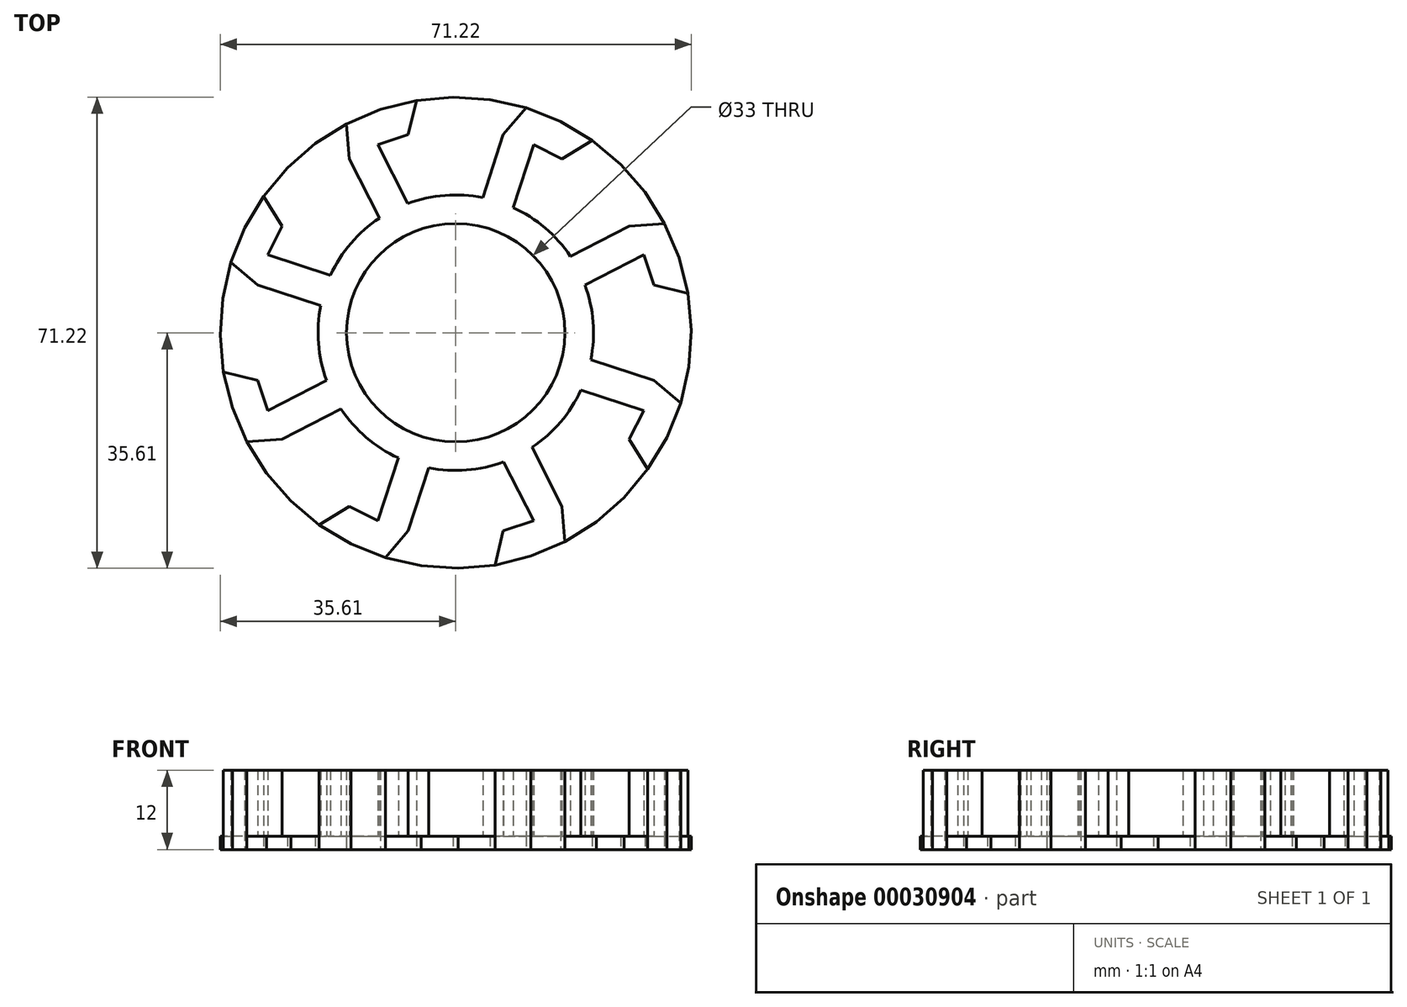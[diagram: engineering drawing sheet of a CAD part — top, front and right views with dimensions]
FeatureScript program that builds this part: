
annotation { "Feature Type Name" : "Feature", "Feature Type Description" : "" }
export const myFeature = defineFeature(function(context is Context, id is Id, definition is map)
    precondition{}
    {
        {
            var Q0;
            Q0=qCreatedBy(makeId("Top.planeOp"),FACE);
            var sketch = newSketch(context, id + "F0", { "sketchPlane" : qUnion([Q0])});
            skCircle(sketch, "E0.cCircle", {"center": v(0, 0) * mm, "radius": 30.68 * mm, "construction": true});
            skLineSegment(sketch, "E0.0", {"start": v(30.68, 2.41) * mm, "end": v(30.68, -2.41) * mm});
            skLineSegment(sketch, "E0.1", {"start": v(30.68, -2.41) * mm, "end": v(29.92, -7.18) * mm});
            skLineSegment(sketch, "E0.2", {"start": v(29.92, -7.18) * mm, "end": v(28.43, -11.78) * mm});
            skLineSegment(sketch, "E0.3", {"start": v(28.43, -11.78) * mm, "end": v(26.24, -16.08) * mm});
            skLineSegment(sketch, "E0.4", {"start": v(26.24, -16.08) * mm, "end": v(23.4, -19.98) * mm});
            skLineSegment(sketch, "E0.5", {"start": v(23.4, -19.98) * mm, "end": v(19.98, -23.4) * mm});
            skLineSegment(sketch, "E0.6", {"start": v(19.98, -23.4) * mm, "end": v(16.08, -26.24) * mm});
            skLineSegment(sketch, "E0.7", {"start": v(16.08, -26.24) * mm, "end": v(11.78, -28.43) * mm});
            skLineSegment(sketch, "E0.8", {"start": v(11.78, -28.43) * mm, "end": v(7.18, -29.92) * mm});
            skLineSegment(sketch, "E0.9", {"start": v(7.18, -29.92) * mm, "end": v(2.41, -30.68) * mm});
            skLineSegment(sketch, "E0.10", {"start": v(2.41, -30.68) * mm, "end": v(-2.41, -30.68) * mm});
            skLineSegment(sketch, "E0.11", {"start": v(-2.41, -30.68) * mm, "end": v(-7.18, -29.92) * mm});
            skLineSegment(sketch, "E0.12", {"start": v(-7.18, -29.92) * mm, "end": v(-11.78, -28.43) * mm});
            skLineSegment(sketch, "E0.13", {"start": v(-11.78, -28.43) * mm, "end": v(-16.08, -26.24) * mm});
            skLineSegment(sketch, "E0.14", {"start": v(-16.08, -26.24) * mm, "end": v(-19.98, -23.4) * mm});
            skLineSegment(sketch, "E0.15", {"start": v(-19.98, -23.4) * mm, "end": v(-23.4, -19.98) * mm});
            skLineSegment(sketch, "E0.16", {"start": v(-23.4, -19.98) * mm, "end": v(-26.24, -16.08) * mm});
            skLineSegment(sketch, "E0.17", {"start": v(-26.24, -16.08) * mm, "end": v(-28.43, -11.78) * mm});
            skLineSegment(sketch, "E0.18", {"start": v(-28.43, -11.78) * mm, "end": v(-29.92, -7.18) * mm});
            skLineSegment(sketch, "E0.19", {"start": v(-29.92, -7.18) * mm, "end": v(-30.68, -2.41) * mm});
            skLineSegment(sketch, "E0.20", {"start": v(-30.68, -2.41) * mm, "end": v(-30.68, 2.41) * mm});
            skLineSegment(sketch, "E0.21", {"start": v(-30.68, 2.41) * mm, "end": v(-29.92, 7.18) * mm});
            skLineSegment(sketch, "E0.22", {"start": v(-29.92, 7.18) * mm, "end": v(-28.43, 11.78) * mm});
            skLineSegment(sketch, "E0.23", {"start": v(-28.43, 11.78) * mm, "end": v(-26.24, 16.08) * mm});
            skLineSegment(sketch, "E0.24", {"start": v(-26.24, 16.08) * mm, "end": v(-23.4, 19.98) * mm});
            skLineSegment(sketch, "E0.25", {"start": v(-23.4, 19.98) * mm, "end": v(-19.98, 23.4) * mm});
            skLineSegment(sketch, "E0.26", {"start": v(-19.98, 23.4) * mm, "end": v(-16.08, 26.24) * mm});
            skLineSegment(sketch, "E0.27", {"start": v(-16.08, 26.24) * mm, "end": v(-11.78, 28.43) * mm});
            skLineSegment(sketch, "E0.28", {"start": v(-11.78, 28.43) * mm, "end": v(-7.18, 29.92) * mm});
            skLineSegment(sketch, "E0.29", {"start": v(-7.18, 29.92) * mm, "end": v(-2.41, 30.68) * mm});
            skLineSegment(sketch, "E0.30", {"start": v(-2.41, 30.68) * mm, "end": v(2.41, 30.68) * mm});
            skLineSegment(sketch, "E0.31", {"start": v(2.41, 30.68) * mm, "end": v(7.18, 29.92) * mm});
            skLineSegment(sketch, "E0.32", {"start": v(7.18, 29.92) * mm, "end": v(11.78, 28.43) * mm});
            skLineSegment(sketch, "E0.33", {"start": v(11.78, 28.43) * mm, "end": v(16.08, 26.24) * mm});
            skLineSegment(sketch, "E0.34", {"start": v(16.08, 26.24) * mm, "end": v(19.98, 23.4) * mm});
            skLineSegment(sketch, "E0.35", {"start": v(19.98, 23.4) * mm, "end": v(23.4, 19.98) * mm});
            skLineSegment(sketch, "E0.36", {"start": v(23.4, 19.98) * mm, "end": v(26.24, 16.08) * mm});
            skLineSegment(sketch, "E0.37", {"start": v(26.24, 16.08) * mm, "end": v(28.43, 11.78) * mm});
            skLineSegment(sketch, "E0.38", {"start": v(28.43, 11.78) * mm, "end": v(29.92, 7.18) * mm});
            skLineSegment(sketch, "E0.39", {"start": v(29.92, 7.18) * mm, "end": v(30.68, 2.41) * mm});
            skPoint(sketch, "E0.0.midPoint", {"position": v(30.68, 0) * mm});
            skCircle(sketch, "E1.cCircle", {"center": v(0, 0) * mm, "radius": 35.5 * mm, "construction": true});
            skLineSegment(sketch, "E1.0", {"start": v(-0.37, 35.61) * mm, "end": v(5.2, 35.23) * mm});
            skLineSegment(sketch, "E1.1", {"start": v(5.2, 35.23) * mm, "end": v(10.65, 33.98) * mm});
            skLineSegment(sketch, "E1.2", {"start": v(10.65, 33.98) * mm, "end": v(15.83, 31.9) * mm});
            skLineSegment(sketch, "E1.3", {"start": v(15.83, 31.9) * mm, "end": v(20.63, 29.03) * mm});
            skLineSegment(sketch, "E1.4", {"start": v(20.63, 29.03) * mm, "end": v(24.92, 25.45) * mm});
            skLineSegment(sketch, "E1.5", {"start": v(24.92, 25.45) * mm, "end": v(28.6, 21.23) * mm});
            skLineSegment(sketch, "E1.6", {"start": v(28.6, 21.23) * mm, "end": v(31.56, 16.5) * mm});
            skLineSegment(sketch, "E1.7", {"start": v(31.56, 16.5) * mm, "end": v(33.75, 11.36) * mm});
            skLineSegment(sketch, "E1.8", {"start": v(33.75, 11.36) * mm, "end": v(35.11, 5.94) * mm});
            skLineSegment(sketch, "E1.9", {"start": v(35.11, 5.94) * mm, "end": v(35.61, 0.37) * mm});
            skLineSegment(sketch, "E1.10", {"start": v(35.61, 0.37) * mm, "end": v(35.23, -5.2) * mm});
            skLineSegment(sketch, "E1.11", {"start": v(35.23, -5.2) * mm, "end": v(33.98, -10.65) * mm});
            skLineSegment(sketch, "E1.12", {"start": v(33.98, -10.65) * mm, "end": v(31.9, -15.83) * mm});
            skLineSegment(sketch, "E1.13", {"start": v(31.9, -15.83) * mm, "end": v(29.03, -20.63) * mm});
            skLineSegment(sketch, "E1.14", {"start": v(29.03, -20.63) * mm, "end": v(25.45, -24.92) * mm});
            skLineSegment(sketch, "E1.15", {"start": v(25.45, -24.92) * mm, "end": v(21.23, -28.6) * mm});
            skLineSegment(sketch, "E1.16", {"start": v(21.23, -28.6) * mm, "end": v(16.5, -31.56) * mm});
            skLineSegment(sketch, "E1.17", {"start": v(16.5, -31.56) * mm, "end": v(11.36, -33.75) * mm});
            skLineSegment(sketch, "E1.18", {"start": v(11.36, -33.75) * mm, "end": v(5.94, -35.11) * mm});
            skLineSegment(sketch, "E1.19", {"start": v(5.94, -35.11) * mm, "end": v(0.37, -35.61) * mm});
            skLineSegment(sketch, "E1.20", {"start": v(0.37, -35.61) * mm, "end": v(-5.2, -35.23) * mm});
            skLineSegment(sketch, "E1.21", {"start": v(-5.2, -35.23) * mm, "end": v(-10.65, -33.98) * mm});
            skLineSegment(sketch, "E1.22", {"start": v(-10.65, -33.98) * mm, "end": v(-15.83, -31.9) * mm});
            skLineSegment(sketch, "E1.23", {"start": v(-15.83, -31.9) * mm, "end": v(-20.63, -29.03) * mm});
            skLineSegment(sketch, "E1.24", {"start": v(-20.63, -29.03) * mm, "end": v(-24.92, -25.45) * mm});
            skLineSegment(sketch, "E1.25", {"start": v(-24.92, -25.45) * mm, "end": v(-28.6, -21.23) * mm});
            skLineSegment(sketch, "E1.26", {"start": v(-28.6, -21.23) * mm, "end": v(-31.56, -16.5) * mm});
            skLineSegment(sketch, "E1.27", {"start": v(-31.56, -16.5) * mm, "end": v(-33.75, -11.36) * mm});
            skLineSegment(sketch, "E1.28", {"start": v(-33.75, -11.36) * mm, "end": v(-35.11, -5.94) * mm});
            skLineSegment(sketch, "E1.29", {"start": v(-35.11, -5.94) * mm, "end": v(-35.61, -0.37) * mm});
            skLineSegment(sketch, "E1.30", {"start": v(-35.61, -0.37) * mm, "end": v(-35.23, 5.2) * mm});
            skLineSegment(sketch, "E1.31", {"start": v(-35.23, 5.2) * mm, "end": v(-33.98, 10.65) * mm});
            skLineSegment(sketch, "E1.32", {"start": v(-33.98, 10.65) * mm, "end": v(-31.9, 15.83) * mm});
            skLineSegment(sketch, "E1.33", {"start": v(-31.9, 15.83) * mm, "end": v(-29.03, 20.63) * mm});
            skLineSegment(sketch, "E1.34", {"start": v(-29.03, 20.63) * mm, "end": v(-25.45, 24.92) * mm});
            skLineSegment(sketch, "E1.35", {"start": v(-25.45, 24.92) * mm, "end": v(-21.23, 28.6) * mm});
            skLineSegment(sketch, "E1.36", {"start": v(-21.23, 28.6) * mm, "end": v(-16.5, 31.56) * mm});
            skLineSegment(sketch, "E1.37", {"start": v(-16.5, 31.56) * mm, "end": v(-11.36, 33.75) * mm});
            skLineSegment(sketch, "E1.38", {"start": v(-11.36, 33.75) * mm, "end": v(-5.94, 35.11) * mm});
            skLineSegment(sketch, "E1.39", {"start": v(-5.94, 35.11) * mm, "end": v(-0.37, 35.61) * mm});
            skPoint(sketch, "E1.0.midPoint", {"position": v(2.41, 35.42) * mm});
            skCircle(sketch, "E2", {"center": v(0, 0) * mm, "radius": 20.82 * mm});
            skCircle(sketch, "E3", {"center": v(0, 0) * mm, "radius": 16.5 * mm});
            skLineSegment(sketch, "E4", {"start": v(7.18, 29.92) * mm, "end": v(10.65, 33.98) * mm});
            skLineSegment(sketch, "E5", {"start": v(16.08, 26.24) * mm, "end": v(20.63, 29.03) * mm});
            skLineSegment(sketch, "E6", {"start": v(26.24, 16.08) * mm, "end": v(31.56, 16.5) * mm});
            skLineSegment(sketch, "E7", {"start": v(29.92, 7.18) * mm, "end": v(35.11, 5.94) * mm});
            skLineSegment(sketch, "E8", {"start": v(29.92, -7.18) * mm, "end": v(33.98, -10.65) * mm});
            skLineSegment(sketch, "E9", {"start": v(26.24, -16.08) * mm, "end": v(29.03, -20.63) * mm});
            skLineSegment(sketch, "E10", {"start": v(16.08, -26.24) * mm, "end": v(16.5, -31.56) * mm});
            skLineSegment(sketch, "E11", {"start": v(7.18, -29.92) * mm, "end": v(5.94, -35.11) * mm});
            skLineSegment(sketch, "E12", {"start": v(-7.18, -29.92) * mm, "end": v(-10.65, -33.98) * mm});
            skLineSegment(sketch, "E13", {"start": v(-16.08, -26.24) * mm, "end": v(-20.63, -29.03) * mm});
            skLineSegment(sketch, "E14", {"start": v(-26.24, -16.08) * mm, "end": v(-31.56, -16.5) * mm});
            skLineSegment(sketch, "E15", {"start": v(-29.92, -7.18) * mm, "end": v(-35.11, -5.94) * mm});
            skLineSegment(sketch, "E16", {"start": v(-29.92, 7.18) * mm, "end": v(-33.98, 10.65) * mm});
            skLineSegment(sketch, "E17", {"start": v(-26.24, 16.08) * mm, "end": v(-29.03, 20.63) * mm});
            skLineSegment(sketch, "E18", {"start": v(-16.08, 26.24) * mm, "end": v(-16.5, 31.56) * mm});
            skLineSegment(sketch, "E19", {"start": v(-7.18, 29.92) * mm, "end": v(-5.94, 35.11) * mm});
            skLineSegment(sketch, "E20", {"start": v(-11.78, 28.43) * mm, "end": v(-7.24, 19.52) * mm});
            skLineSegment(sketch, "E21", {"start": v(-16.08, 26.24) * mm, "end": v(-11.54, 17.33) * mm});
            skLineSegment(sketch, "E22", {"start": v(-28.43, 11.78) * mm, "end": v(-18.92, 8.69) * mm});
            skLineSegment(sketch, "E23", {"start": v(-29.92, 7.18) * mm, "end": v(-20.4, 4.1) * mm});
            skLineSegment(sketch, "E24", {"start": v(-28.43, -11.78) * mm, "end": v(-19.52, -7.24) * mm});
            skLineSegment(sketch, "E25", {"start": v(-26.24, -16.08) * mm, "end": v(-17.33, -11.54) * mm});
            skLineSegment(sketch, "E26", {"start": v(-7.18, -29.92) * mm, "end": v(-4.1, -20.4) * mm});
            skLineSegment(sketch, "E27", {"start": v(-11.78, -28.43) * mm, "end": v(-8.69, -18.92) * mm});
            skLineSegment(sketch, "E28", {"start": v(16.08, -26.24) * mm, "end": v(11.54, -17.33) * mm});
            skLineSegment(sketch, "E29", {"start": v(11.78, -28.43) * mm, "end": v(7.24, -19.52) * mm});
            skLineSegment(sketch, "E30", {"start": v(29.92, -7.18) * mm, "end": v(20.4, -4.1) * mm});
            skLineSegment(sketch, "E31", {"start": v(28.43, -11.78) * mm, "end": v(18.92, -8.69) * mm});
            skLineSegment(sketch, "E32", {"start": v(28.43, 11.78) * mm, "end": v(19.52, 7.24) * mm});
            skLineSegment(sketch, "E33", {"start": v(26.24, 16.08) * mm, "end": v(17.33, 11.54) * mm});
            skLineSegment(sketch, "E34", {"start": v(11.78, 28.43) * mm, "end": v(8.69, 18.92) * mm});
            skLineSegment(sketch, "E35", {"start": v(7.18, 29.92) * mm, "end": v(4.1, 20.4) * mm});
            skSolve(sketch);
        }
        {
            var Q0;
            Q0=makeQuery(id+"F0.imprint","IMPRINT",FACE,{"disambiguationData":[TD([[makeQuery(id+"F0.imprint","IMPRINT",EDGE,{"derivedFrom":sQuery(id+"F0.wireOp",EDGE,"E0.23")}),-1.0]])]});
            var sketch = newSketch(context, id + "F1", { "sketchPlane" : qUnion([Q0])});
            skSolve(sketch);
        }
        {
            var Q0;
            Q0=makeQuery(id+"F0.imprint","IMPRINT",FACE,{"disambiguationData":[TD([[makeQuery(id+"F0.imprint","IMPRINT",EDGE,{"derivedFrom":sQuery(id+"F0.wireOp",EDGE,"E0.18")}),-1.0]])]});
            var sketch = newSketch(context, id + "F2", { "sketchPlane" : qUnion([Q0])});
            skSolve(sketch);
        }
        {
            var Q0;
            Q0=makeQuery(id+"F0.imprint","IMPRINT",FACE,{"disambiguationData":[TD([[makeQuery(id+"F0.imprint","IMPRINT",EDGE,{"derivedFrom":sQuery(id+"F0.wireOp",EDGE,"E0.13")}),-1.0]])]});
            var sketch = newSketch(context, id + "F3", { "sketchPlane" : qUnion([Q0])});
            skSolve(sketch);
        }
        {
            var Q0;
            Q0=makeQuery(id+"F0.imprint","IMPRINT",FACE,{"disambiguationData":[TD([[makeQuery(id+"F0.imprint","IMPRINT",EDGE,{"derivedFrom":sQuery(id+"F0.wireOp",EDGE,"E0.8")}),-1.0]])]});
            var sketch = newSketch(context, id + "F4", { "sketchPlane" : qUnion([Q0])});
            skSolve(sketch);
        }
        {
            var Q0;
            Q0=makeQuery(id+"F0.imprint","IMPRINT",FACE,{"disambiguationData":[TD([[makeQuery(id+"F0.imprint","IMPRINT",EDGE,{"derivedFrom":sQuery(id+"F0.wireOp",EDGE,"E0.3")}),-1.0]])]});
            var sketch = newSketch(context, id + "F5", { "sketchPlane" : qUnion([Q0])});
            skSolve(sketch);
        }
        {
            var Q0;
            Q0=makeQuery(id+"F0.imprint","IMPRINT",FACE,{"disambiguationData":[TD([[makeQuery(id+"F0.imprint","IMPRINT",EDGE,{"derivedFrom":sQuery(id+"F0.wireOp",EDGE,"E0.0")}),-1.0]])]});
            var sketch = newSketch(context, id + "F6", { "sketchPlane" : qUnion([Q0])});
            skSolve(sketch);
        }
        {
            var Q0;
            Q0=makeQuery(id+"F0.imprint","IMPRINT",FACE,{"disambiguationData":[TD([[makeQuery(id+"F0.imprint","IMPRINT",EDGE,{"derivedFrom":sQuery(id+"F0.wireOp",EDGE,"E0.33")}),-1.0]])]});
            var sketch = newSketch(context, id + "F7", { "sketchPlane" : qUnion([Q0])});
            skSolve(sketch);
        }
        {
            var Q0;
            Q0=makeQuery(id+"F0.imprint","IMPRINT",FACE,{"disambiguationData":[TD([[makeQuery(id+"F0.imprint","IMPRINT",EDGE,{"derivedFrom":sQuery(id+"F0.wireOp",EDGE,"E0.28")}),-1.0]])]});
            var sketch = newSketch(context, id + "F8", { "sketchPlane" : qUnion([Q0])});
            skSolve(sketch);
        }
        {
            var Q0;
            Q0=makeQuery(id+"F0.imprint","IMPRINT",FACE,{"disambiguationData":[TD([[makeQuery(id+"F0.imprint","IMPRINT",EDGE,{"derivedFrom":sQuery(id+"F0.wireOp",EDGE,"E0.24")}),1.0]])]});
            var sketch = newSketch(context, id + "F9", { "sketchPlane" : qUnion([Q0])});
            skSolve(sketch);
        }
        {
            var Q0;
            Q0=makeQuery(id+"F0.imprint","IMPRINT",FACE,{"disambiguationData":[TD([[makeQuery(id+"F0.imprint","IMPRINT",EDGE,{"derivedFrom":sQuery(id+"F0.wireOp",EDGE,"E0.29")}),1.0]])]});
            var sketch = newSketch(context, id + "F10", { "sketchPlane" : qUnion([Q0])});
            skSolve(sketch);
        }
        {
            var Q0;
            Q0=makeQuery(id+"F0.imprint","IMPRINT",FACE,{"disambiguationData":[TD([[makeQuery(id+"F0.imprint","IMPRINT",EDGE,{"derivedFrom":sQuery(id+"F0.wireOp",EDGE,"E0.34")}),1.0]])]});
            var sketch = newSketch(context, id + "F11", { "sketchPlane" : qUnion([Q0])});
            skSolve(sketch);
        }
        {
            var Q0;
            Q0=makeQuery(id+"F0.imprint","IMPRINT",FACE,{"disambiguationData":[TD([[makeQuery(id+"F0.imprint","IMPRINT",EDGE,{"derivedFrom":sQuery(id+"F0.wireOp",EDGE,"E0.0")}),1.0]])]});
            var sketch = newSketch(context, id + "F12", { "sketchPlane" : qUnion([Q0])});
            skSolve(sketch);
        }
        {
            var Q0;
            Q0=makeQuery(id+"F0.imprint","IMPRINT",FACE,{"disambiguationData":[TD([[makeQuery(id+"F0.imprint","IMPRINT",EDGE,{"derivedFrom":sQuery(id+"F0.wireOp",EDGE,"E0.4")}),1.0]])]});
            var sketch = newSketch(context, id + "F13", { "sketchPlane" : qUnion([Q0])});
            skSolve(sketch);
        }
        {
            var Q0;
            Q0=makeQuery(id+"F0.imprint","IMPRINT",FACE,{"disambiguationData":[TD([[makeQuery(id+"F0.imprint","IMPRINT",EDGE,{"derivedFrom":sQuery(id+"F0.wireOp",EDGE,"E0.9")}),1.0]])]});
            var sketch = newSketch(context, id + "F14", { "sketchPlane" : qUnion([Q0])});
            skSolve(sketch);
        }
        {
            var Q0;
            Q0=makeQuery(id+"F0.imprint","IMPRINT",FACE,{"disambiguationData":[TD([[makeQuery(id+"F0.imprint","IMPRINT",EDGE,{"derivedFrom":sQuery(id+"F0.wireOp",EDGE,"E0.14")}),1.0]])]});
            var sketch = newSketch(context, id + "F15", { "sketchPlane" : qUnion([Q0])});
            skSolve(sketch);
        }
        {
            var Q0;
            Q0=makeQuery(id+"F0.imprint","IMPRINT",FACE,{"disambiguationData":[TD([[makeQuery(id+"F0.imprint","IMPRINT",EDGE,{"derivedFrom":sQuery(id+"F0.wireOp",EDGE,"E0.19")}),1.0]])]});
            var sketch = newSketch(context, id + "F16", { "sketchPlane" : qUnion([Q0])});
            skSolve(sketch);
        }
        {
            var Q0;
            Q0=makeQuery(id+"F0.imprint","IMPRINT",FACE,{"disambiguationData":[TD([[makeQuery(id+"F0.imprint","IMPRINT",EDGE,{"derivedFrom":sQuery(id+"F0.wireOp",EDGE,"E3")}),-1.0]])]});
            var Q1;
            Q1=makeQuery(id+"F0.imprint","IMPRINT",FACE,{"disambiguationData":[TD([[makeQuery(id+"F0.imprint","IMPRINT",EDGE,{"derivedFrom":sQuery(id+"F0.wireOp",EDGE,"E0.32")}),-1.0]])]});
            var Q2;
            Q2=makeQuery(id+"F0.imprint","IMPRINT",FACE,{"disambiguationData":[TD([[makeQuery(id+"F0.imprint","IMPRINT",EDGE,{"derivedFrom":sQuery(id+"F0.wireOp",EDGE,"E0.32")}),1.0]])]});
            var Q3;
            Q3=makeQuery(id+"F0.imprint","IMPRINT",FACE,{"disambiguationData":[TD([[makeQuery(id+"F0.imprint","IMPRINT",EDGE,{"derivedFrom":sQuery(id+"F0.wireOp",EDGE,"E0.27")}),1.0]])]});
            var Q4;
            Q4=makeQuery(id+"F0.imprint","IMPRINT",FACE,{"disambiguationData":[TD([[makeQuery(id+"F0.imprint","IMPRINT",EDGE,{"derivedFrom":sQuery(id+"F0.wireOp",EDGE,"E0.27")}),-1.0]])]});
            var Q5;
            Q5=makeQuery(id+"F0.imprint","IMPRINT",FACE,{"disambiguationData":[TD([[makeQuery(id+"F0.imprint","IMPRINT",EDGE,{"derivedFrom":sQuery(id+"F0.wireOp",EDGE,"E0.22")}),1.0]])]});
            var Q6;
            Q6=makeQuery(id+"F0.imprint","IMPRINT",FACE,{"disambiguationData":[TD([[makeQuery(id+"F0.imprint","IMPRINT",EDGE,{"derivedFrom":sQuery(id+"F0.wireOp",EDGE,"E0.22")}),-1.0]])]});
            var Q7;
            Q7=makeQuery(id+"F0.imprint","IMPRINT",FACE,{"disambiguationData":[TD([[makeQuery(id+"F0.imprint","IMPRINT",EDGE,{"derivedFrom":sQuery(id+"F0.wireOp",EDGE,"E0.17")}),1.0]])]});
            var Q8;
            Q8=makeQuery(id+"F0.imprint","IMPRINT",FACE,{"disambiguationData":[TD([[makeQuery(id+"F0.imprint","IMPRINT",EDGE,{"derivedFrom":sQuery(id+"F0.wireOp",EDGE,"E0.17")}),-1.0]])]});
            var Q9;
            Q9=makeQuery(id+"F0.imprint","IMPRINT",FACE,{"disambiguationData":[TD([[makeQuery(id+"F0.imprint","IMPRINT",EDGE,{"derivedFrom":sQuery(id+"F0.wireOp",EDGE,"E0.12")}),1.0]])]});
            var Q10;
            Q10=makeQuery(id+"F0.imprint","IMPRINT",FACE,{"disambiguationData":[TD([[makeQuery(id+"F0.imprint","IMPRINT",EDGE,{"derivedFrom":sQuery(id+"F0.wireOp",EDGE,"E0.12")}),-1.0]])]});
            var Q11;
            Q11=makeQuery(id+"F0.imprint","IMPRINT",FACE,{"disambiguationData":[TD([[makeQuery(id+"F0.imprint","IMPRINT",EDGE,{"derivedFrom":sQuery(id+"F0.wireOp",EDGE,"E0.7")}),1.0]])]});
            var Q12;
            Q12=makeQuery(id+"F0.imprint","IMPRINT",FACE,{"disambiguationData":[TD([[makeQuery(id+"F0.imprint","IMPRINT",EDGE,{"derivedFrom":sQuery(id+"F0.wireOp",EDGE,"E0.7")}),-1.0]])]});
            var Q13;
            Q13=makeQuery(id+"F0.imprint","IMPRINT",FACE,{"disambiguationData":[TD([[makeQuery(id+"F0.imprint","IMPRINT",EDGE,{"derivedFrom":sQuery(id+"F0.wireOp",EDGE,"E0.2")}),1.0]])]});
            var Q14;
            Q14=makeQuery(id+"F0.imprint","IMPRINT",FACE,{"disambiguationData":[TD([[makeQuery(id+"F0.imprint","IMPRINT",EDGE,{"derivedFrom":sQuery(id+"F0.wireOp",EDGE,"E0.2")}),-1.0]])]});
            var Q15;
            Q15=makeQuery(id+"F0.imprint","IMPRINT",FACE,{"disambiguationData":[TD([[makeQuery(id+"F0.imprint","IMPRINT",EDGE,{"derivedFrom":sQuery(id+"F0.wireOp",EDGE,"E0.37")}),1.0]])]});
            var Q16;
            Q16=makeQuery(id+"F0.imprint","IMPRINT",FACE,{"disambiguationData":[TD([[makeQuery(id+"F0.imprint","IMPRINT",EDGE,{"derivedFrom":sQuery(id+"F0.wireOp",EDGE,"E0.37")}),-1.0]])]});
            extrude(context, id + "F17", {"entities" : qUnion([Q0, Q1, Q2, Q3, Q4, Q5, Q6, Q7, Q8, Q9, Q10, Q11, Q12, Q13, Q14, Q15, Q16]), "depth" : 12 * mm});
        }
        {
            var Q0;
            Q0=makeQuery(id+"F9.imprint","IMPRINT",FACE,{"disambiguationData":[TD([[makeQuery(id+"F9.imprint","IMPRINT",EDGE,{"derivedFrom":makeQuery(id+"F0.imprint","IMPRINT",EDGE,{"derivedFrom":sQuery(id+"F0.wireOp",EDGE,"E0.24")})}),1.0]])]});
            var Q1;
            Q1=makeQuery(id+"F10.imprint","IMPRINT",FACE,{"disambiguationData":[TD([[makeQuery(id+"F10.imprint","IMPRINT",EDGE,{"derivedFrom":makeQuery(id+"F0.imprint","IMPRINT",EDGE,{"derivedFrom":sQuery(id+"F0.wireOp",EDGE,"E0.29")})}),1.0]])]});
            var Q2;
            Q2=makeQuery(id+"F11.imprint","IMPRINT",FACE,{"disambiguationData":[TD([[makeQuery(id+"F11.imprint","IMPRINT",EDGE,{"derivedFrom":makeQuery(id+"F0.imprint","IMPRINT",EDGE,{"derivedFrom":sQuery(id+"F0.wireOp",EDGE,"E0.34")})}),1.0]])]});
            var Q3;
            Q3=makeQuery(id+"F7.imprint","IMPRINT",FACE,{"disambiguationData":[TD([[makeQuery(id+"F7.imprint","IMPRINT",EDGE,{"derivedFrom":makeQuery(id+"F0.imprint","IMPRINT",EDGE,{"derivedFrom":sQuery(id+"F0.wireOp",EDGE,"E0.33")})}),-1.0]])]});
            var Q4;
            Q4=makeQuery(id+"F8.imprint","IMPRINT",FACE,{"disambiguationData":[TD([[makeQuery(id+"F8.imprint","IMPRINT",EDGE,{"derivedFrom":makeQuery(id+"F0.imprint","IMPRINT",EDGE,{"derivedFrom":sQuery(id+"F0.wireOp",EDGE,"E0.28")})}),-1.0]])]});
            var Q5;
            Q5=makeQuery(id+"F1.imprint","IMPRINT",FACE,{"disambiguationData":[TD([[makeQuery(id+"F1.imprint","IMPRINT",EDGE,{"derivedFrom":makeQuery(id+"F0.imprint","IMPRINT",EDGE,{"derivedFrom":sQuery(id+"F0.wireOp",EDGE,"E0.23")})}),-1.0]])]});
            var Q6;
            Q6=makeQuery(id+"F2.imprint","IMPRINT",FACE,{"disambiguationData":[TD([[makeQuery(id+"F2.imprint","IMPRINT",EDGE,{"derivedFrom":makeQuery(id+"F0.imprint","IMPRINT",EDGE,{"derivedFrom":sQuery(id+"F0.wireOp",EDGE,"E0.18")})}),-1.0]])]});
            var Q7;
            Q7=makeQuery(id+"F16.imprint","IMPRINT",FACE,{"disambiguationData":[TD([[makeQuery(id+"F16.imprint","IMPRINT",EDGE,{"derivedFrom":makeQuery(id+"F0.imprint","IMPRINT",EDGE,{"derivedFrom":sQuery(id+"F0.wireOp",EDGE,"E0.19")})}),1.0]])]});
            var Q8;
            Q8=makeQuery(id+"F15.imprint","IMPRINT",FACE,{"disambiguationData":[TD([[makeQuery(id+"F15.imprint","IMPRINT",EDGE,{"derivedFrom":makeQuery(id+"F0.imprint","IMPRINT",EDGE,{"derivedFrom":sQuery(id+"F0.wireOp",EDGE,"E0.14")})}),1.0]])]});
            var Q9;
            Q9=makeQuery(id+"F3.imprint","IMPRINT",FACE,{"disambiguationData":[TD([[makeQuery(id+"F3.imprint","IMPRINT",EDGE,{"derivedFrom":makeQuery(id+"F0.imprint","IMPRINT",EDGE,{"derivedFrom":sQuery(id+"F0.wireOp",EDGE,"E0.13")})}),-1.0]])]});
            var Q10;
            Q10=makeQuery(id+"F14.imprint","IMPRINT",FACE,{"disambiguationData":[TD([[makeQuery(id+"F14.imprint","IMPRINT",EDGE,{"derivedFrom":makeQuery(id+"F0.imprint","IMPRINT",EDGE,{"derivedFrom":sQuery(id+"F0.wireOp",EDGE,"E0.9")})}),1.0]])]});
            var Q11;
            Q11=makeQuery(id+"F4.imprint","IMPRINT",FACE,{"disambiguationData":[TD([[makeQuery(id+"F4.imprint","IMPRINT",EDGE,{"derivedFrom":makeQuery(id+"F0.imprint","IMPRINT",EDGE,{"derivedFrom":sQuery(id+"F0.wireOp",EDGE,"E0.8")})}),-1.0]])]});
            var Q12;
            Q12=makeQuery(id+"F13.imprint","IMPRINT",FACE,{"disambiguationData":[TD([[makeQuery(id+"F13.imprint","IMPRINT",EDGE,{"derivedFrom":makeQuery(id+"F0.imprint","IMPRINT",EDGE,{"derivedFrom":sQuery(id+"F0.wireOp",EDGE,"E0.4")})}),1.0]])]});
            var Q13;
            Q13=makeQuery(id+"F5.imprint","IMPRINT",FACE,{"disambiguationData":[TD([[makeQuery(id+"F5.imprint","IMPRINT",EDGE,{"derivedFrom":makeQuery(id+"F0.imprint","IMPRINT",EDGE,{"derivedFrom":sQuery(id+"F0.wireOp",EDGE,"E0.3")})}),-1.0]])]});
            var Q14;
            Q14=makeQuery(id+"F12.imprint","IMPRINT",FACE,{"disambiguationData":[TD([[makeQuery(id+"F12.imprint","IMPRINT",EDGE,{"derivedFrom":makeQuery(id+"F0.imprint","IMPRINT",EDGE,{"derivedFrom":sQuery(id+"F0.wireOp",EDGE,"E0.0")})}),1.0]])]});
            var Q15;
            Q15=makeQuery(id+"F6.imprint","IMPRINT",FACE,{"disambiguationData":[TD([[makeQuery(id+"F6.imprint","IMPRINT",EDGE,{"derivedFrom":makeQuery(id+"F0.imprint","IMPRINT",EDGE,{"derivedFrom":sQuery(id+"F0.wireOp",EDGE,"E0.0")})}),-1.0]])]});
            extrude(context, id + "F18", {"entities" : qUnion([Q0, Q1, Q2, Q3, Q4, Q5, Q6, Q7, Q8, Q9, Q10, Q11, Q12, Q13, Q14, Q15]), "operationType" : NewBodyOperationType.ADD, "depth" : 2 * mm});
        }
    });
